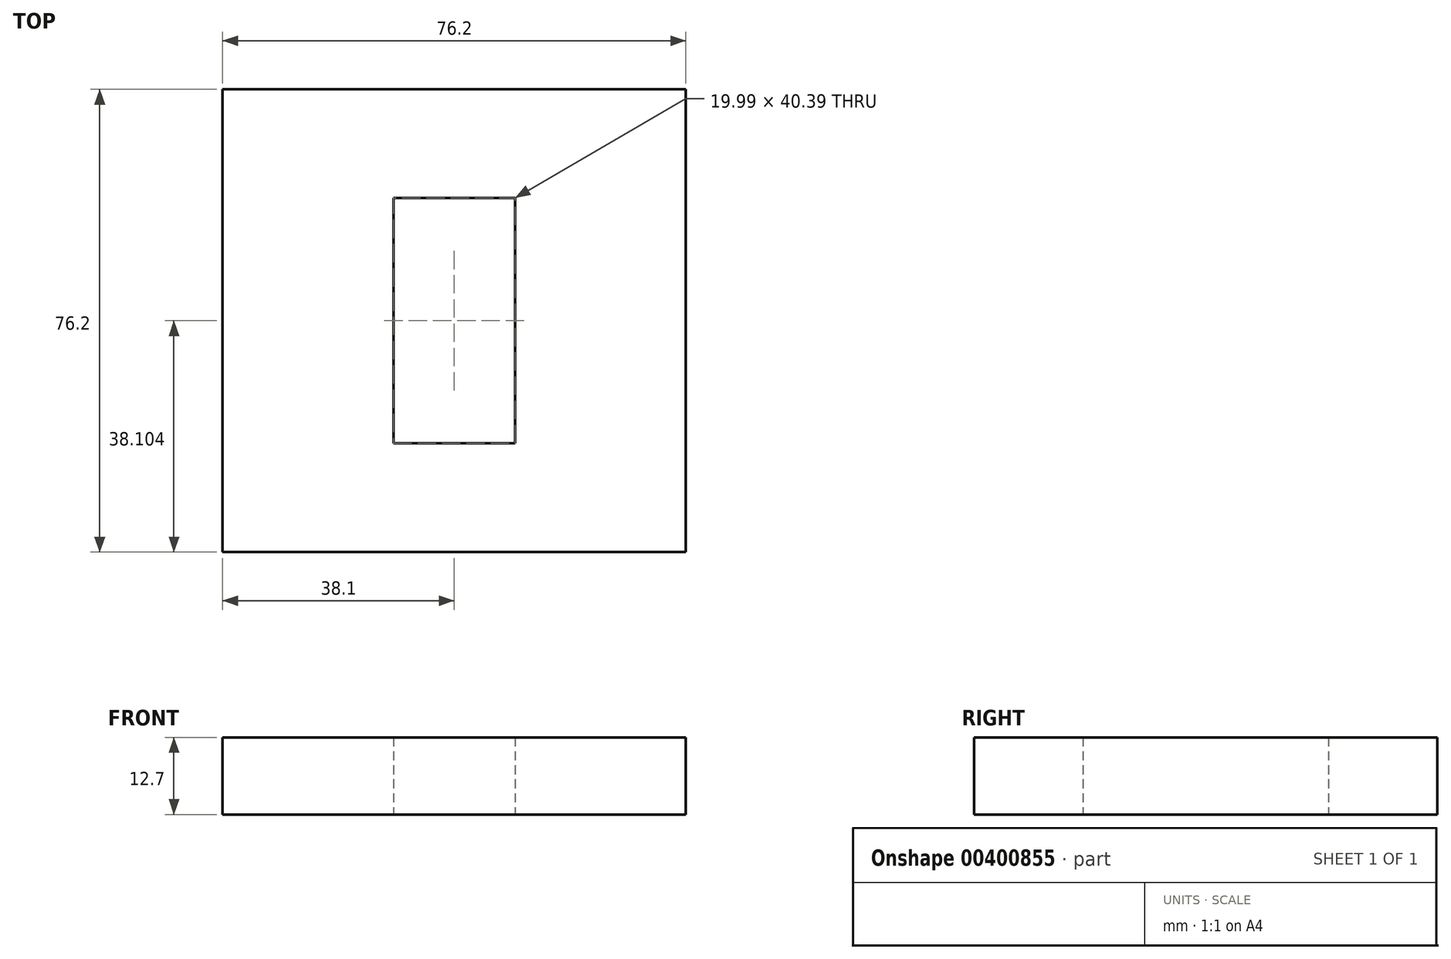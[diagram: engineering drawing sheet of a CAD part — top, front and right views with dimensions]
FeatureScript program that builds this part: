
annotation { "Feature Type Name" : "Feature", "Feature Type Description" : "" }
export const myFeature = defineFeature(function(context is Context, id is Id, definition is map)
    precondition{}
    {
        {
            var Q0;
            Q0=qCreatedBy(makeId("Top.planeOp"),FACE);
            var sketch = newSketch(context, id + "F0", { "sketchPlane" : qUnion([Q0])});
            skLineSegment(sketch, "E0", {"start": v(0, -4.96) * mm, "end": v(0, 71.24) * mm});
            skLineSegment(sketch, "E1", {"start": v(0, 71.24) * mm, "end": v(76.2, 71.24) * mm});
            skLineSegment(sketch, "E2", {"start": v(0, -4.96) * mm, "end": v(76.2, -4.96) * mm});
            skLineSegment(sketch, "E3", {"start": v(76.2, -4.96) * mm, "end": v(76.2, 71.24) * mm});
            skPoint(sketch, "E4.endSnap0", {"position": v(38.1, 71.24) * mm});
            skLineSegment(sketch, "E5", {"start": v(28.1, 53.34) * mm, "end": v(28.1, 33.14) * mm});
            skLineSegment(sketch, "E6", {"start": v(28.1, 53.34) * mm, "end": v(38.1, 53.34) * mm});
            skLineSegment(sketch, "E7", {"start": v(28.1, 12.95) * mm, "end": v(28.1, 33.14) * mm});
            skLineSegment(sketch, "E8", {"start": v(28.1, 12.95) * mm, "end": v(38.1, 12.95) * mm});
            skLineSegment(sketch, "E9", {"start": v(38.1, 12.95) * mm, "end": v(48.1, 12.95) * mm});
            skLineSegment(sketch, "E10", {"start": v(48.1, 12.95) * mm, "end": v(48.1, 33.14) * mm});
            skLineSegment(sketch, "E11", {"start": v(48.1, 53.34) * mm, "end": v(38.1, 53.34) * mm});
            skLineSegment(sketch, "E12", {"start": v(48.1, 33.14) * mm, "end": v(48.1, 53.34) * mm});
            skSolve(sketch);
        }
        {
            var Q0;
            Q0=makeQuery(id+"F0.imprint","IMPRINT",FACE,{"disambiguationData":[TD([[makeQuery(id+"F0.imprint","IMPRINT",EDGE,{"derivedFrom":sQuery(id+"F0.wireOp",EDGE,"E0")}),-1.0]])]});
            extrude(context, id + "F1", {"entities" : qUnion([Q0]), "depth" : 12.7 * mm});
        }
    });
